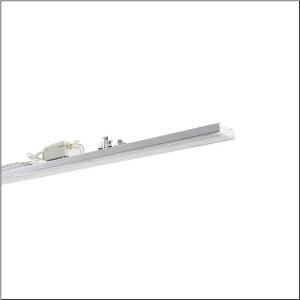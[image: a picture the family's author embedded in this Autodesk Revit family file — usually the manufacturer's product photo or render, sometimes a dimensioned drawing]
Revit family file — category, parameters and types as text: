
# Revit family: licross_11_recessed_ho_51te18dv4m1m
name_source: partatom
category: Lighting Fixtures
units: mm (PartAtom-declared; Revit-internal decimal feet)

## family parameters
Cut with Voids When Loaded = No
Host = Face
Light Source = No
Part Type = Normal
Room Calculation Point = No
Round Connector Dimension = Use Diameter
Shared = No

## types (1)
- --- (1 x LED, 26860 lm, 150.5 W, 4000K)
    Apparent Load = 150 VA
    CIE Flux Codes = 78 94 99 100 100
    Color Rendering = 80
    Color Temperature = 4000K
    Default Elevation = 1800 mm
    Description = Licross 11 Recessed HO, luminaire insert, of sheet steel, galvanised, coil coated, white, length: 2.250mm, width: 66mm, height: 67mm, LED rated luminous flux: 26.870lm, light colour: 840, SDCM (Standard Deviation of Colour Matching)MacAdam ≤ 2 SDCM (initial), control gear: DALI 2, with plug, 5-pole, with phase selection, mains connection: 220..240V, AC, 50/60Hz, rated input power: 151W, internal wiring halogen-free, primary light control with lens, of plastic, primary optical cover: cover, of PMMA, light emission: direct distribution, primary light characteristic: symmetric, protection rating (complete): IP54, insulation class (complete): insulation class I (protective earthing), certification: CE, ENEC, VDE, UKCA, protection symbol: D if used in an environment with non-conductive dust loads with corresponding accessories, impact resistance: IK06, permissible ambient temperature for indoor applications: -40..+35°C, corresponds to IFS (International Featured Standards) requirements for safety and quality in the food industry, reducing of maximum allowable ambient temperature of 5°C with ceiling mounting, LABS conformity tested according to VDMA 24364:2018-05, The light source and the operating device comply with the requirements of the Ecodesign Regulation (EU) 2019/2020 and are replaceable in accordance with this regulation, packaging unit: 1 piece
    Height = 58 mm
    Lamp = 1 x LED
    Lamp Light Flux = 26860 lm
    Lamp Power = 150.5 W
    Lamp count = 1
    Length = 2250 mm
    Luminous efficacy = 178 lm/W
    Manufacturer = Siteco
    ModVariant = No
    Model = 51TE18DV4M1M
    Mounting Place = Ceiling
    Mounting Type = Pendant
    Number of Poles = 1
    OnlyDefault = Yes
    Power Factor = 1
    Product Name = Licross 11 Recessed HO
    Product group = luminaire insert | ceiling pendant
    ProductGroupID = 901
    Protection Class = Protection class I
    Protection Degree = IP 54
    RLX_Detail_Level = 1
    RLX_Emergency_Light_Flux = 0 lm
    RLX_Emergency_Type = 0
    RLX_Emergency_Type_DB = No
    RlxData = <blob elided: 30053 chars, md5=971f86fa>
    Socket = socket
    Standby Power = 0 W
    System Light Flux = 26860 lm
    System Power = 150 W
    Type Comments = factory setting: luminous flux: 100 % | dim-lin: 254 | 690 mA
    Type Image = l_1296930.jpg
    URL = http://relux.com
    VarID = @adj_102373
    Voltage = 0 V
    Weight = 0.00 kg
    Width = 66 mm

## geometry (parser evidence)
native form markers: Blend x4, Sweep x9
no freeform markers — native parametric forms only
